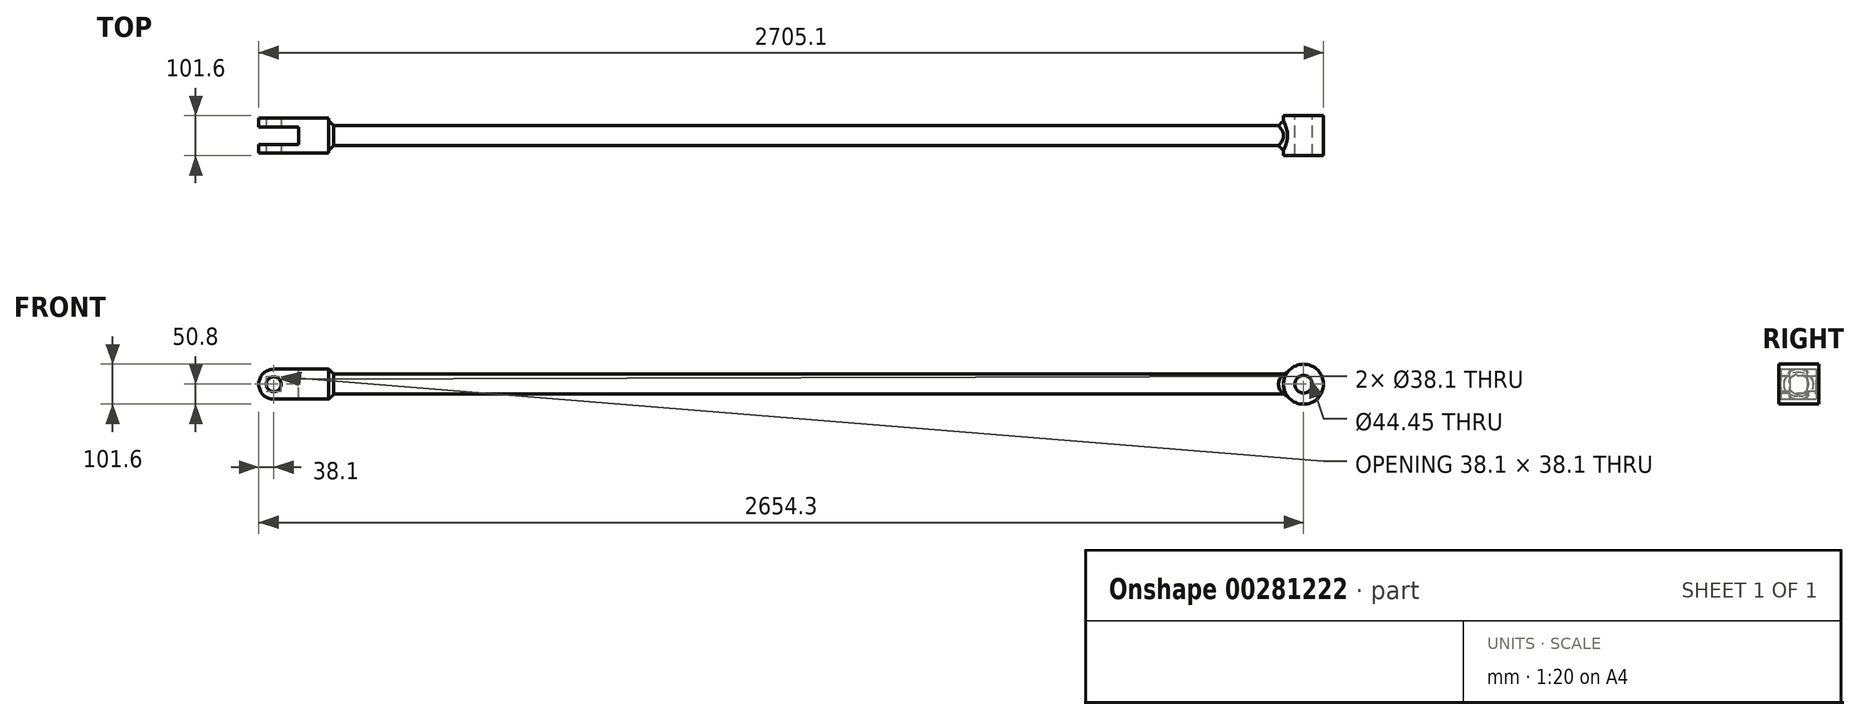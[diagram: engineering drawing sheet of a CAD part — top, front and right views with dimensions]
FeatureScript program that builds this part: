
annotation { "Feature Type Name" : "Feature", "Feature Type Description" : "" }
export const myFeature = defineFeature(function(context is Context, id is Id, definition is map)
    precondition{}
    {
        {
            var Q0;
            Q0=qCreatedBy(makeId("Front.planeOp"),FACE);
            var sketch = newSketch(context, id + "F0", { "sketchPlane" : qUnion([Q0])});
            skCircle(sketch, "E0", {"center": v(0, 0) * mm, "radius": 22.23 * mm});
            skCircle(sketch, "E1", {"center": v(0, 0) * mm, "radius": 50.8 * mm});
            skSolve(sketch);
        }
        {
            var Q0;
            Q0 = qSketchRegion(id + "F0", true);
            extrude(context, id + "F1", {"entities" : qUnion([Q0]), "endBound" : BoundingType.SYMMETRIC, "depth" : 101.6 * mm});
        }
        {
            var Q0;
            Q0=qCreatedBy(makeId("Right.planeOp"),FACE);
            var sketch = newSketch(context, id + "F2", { "sketchPlane" : qUnion([Q0])});
            skCircle(sketch, "E2", {"center": v(0, 0) * mm, "radius": 25.4 * mm});
            skSolve(sketch);
        }
        {
            var Q0;
            Q0 = qSketchRegion(id + "F2", true);
            extrude(context, id + "F3", {"entities" : qUnion([Q0]), "operationType" : NewBodyOperationType.ADD, "oppositeDirection" : true, "depth" : 2616.2 * mm});
        }
        {
            var Q0;
            Q0=qCreatedBy(makeId("Front.planeOp"),FACE);
            var sketch = newSketch(context, id + "F4", { "sketchPlane" : qUnion([Q0])});
            skLineSegment(sketch, "E3.0", {"start": v(-2616.2, 38.1) * mm, "end": v(-2616.2, -38.1) * mm, "construction": true});
            skCircle(sketch, "E4", {"center": v(-2616.2, 0) * mm, "radius": 38.1 * mm});
            skPoint(sketch, "E5.orphan", {"position": v(-2616.2, 25.4) * mm});
            skPoint(sketch, "E6.orphan", {"position": v(-2616.2, -25.4) * mm});
            skLineSegment(sketch, "E7.bottom", {"start": v(-2616.2, 38.1) * mm, "end": v(-2476.5, 38.1) * mm});
            skLineSegment(sketch, "E7.top", {"start": v(-2616.2, -38.1) * mm, "end": v(-2476.5, -38.1) * mm});
            skLineSegment(sketch, "E7.left", {"start": v(-2616.2, 38.1) * mm, "end": v(-2616.2, -38.1) * mm});
            skLineSegment(sketch, "E7.right", {"start": v(-2476.5, 38.1) * mm, "end": v(-2476.5, -38.1) * mm});
            skSolve(sketch);
        }
        {
            var Q0;
            Q0 = qSketchRegion(id + "F4", true);
            extrude(context, id + "F5", {"entities" : qUnion([Q0]), "operationType" : NewBodyOperationType.ADD, "endBound" : BoundingType.SYMMETRIC, "depth" : 88.9 * mm});
        }
        {
            var Q0;
            Q0=makeQuery(id+"F5.opExtrude","CAP_FACE",FACE,{"disambiguationData":[OSD([sQuery(id+"F4.wireOp",EDGE,"E4"),sQuery(id+"F4.wireOp",EDGE,"E7.bottom"),sQuery(id+"F4.wireOp",EDGE,"E7.top"),sQuery(id+"F4.wireOp",EDGE,"E7.right")])],"isStart":false});
            var sketch = newSketch(context, id + "F6", { "sketchPlane" : qUnion([Q0])});
            skArc(sketch, "E8.0.0", {"start": v(-2616.2, 38.1) * mm, "mid": v(-2654.3, 0) * mm, "end": v(-2616.2, -38.1) * mm, "construction": true});
            skLineSegment(sketch, "E8.0.1", {"start": v(-2616.2, -38.1) * mm, "end": v(-2476.5, -38.1) * mm, "construction": true});
            skLineSegment(sketch, "E8.0.2", {"start": v(-2476.5, -38.1) * mm, "end": v(-2476.5, 38.1) * mm, "construction": true});
            skLineSegment(sketch, "E8.0.3", {"start": v(-2476.5, 38.1) * mm, "end": v(-2616.2, 38.1) * mm, "construction": true});
            skCircle(sketch, "E9", {"center": v(-2616.2, 0) * mm, "radius": 19.05 * mm});
            skSolve(sketch);
        }
        {
            var Q0;
            Q0 = qSketchRegion(id + "F6", true);
            extrude(context, id + "F7", {"entities" : qUnion([Q0]), "operationType" : NewBodyOperationType.REMOVE, "endBound" : BoundingType.THROUGH_ALL, "oppositeDirection" : true, "depth" : 25.4 * mm});
        }
        {
            var Q0;
            Q0=makeQuery(id+"F5.opExtrude","SWEPT_FACE",FACE,{"disambiguationData":[OSD([sQuery(id+"F4.wireOp",EDGE,"E7.bottom")])]});
            var sketch = newSketch(context, id + "F8", { "sketchPlane" : qUnion([Q0])});
            skLineSegment(sketch, "E10", {"start": v(-2635.25, -44.45) * mm, "end": v(-2635.25, 44.45) * mm, "construction": true});
            skLineSegment(sketch, "E11", {"start": v(-2597.15, 44.45) * mm, "end": v(-2597.15, -44.45) * mm, "construction": true});
            skLineSegment(sketch, "E12", {"start": v(-2635.25, 0) * mm, "end": v(-2597.15, 0) * mm, "construction": true});
            skLineSegment(sketch, "E13", {"start": v(-2616.2, 0) * mm, "end": v(-2616.2, 76.94) * mm, "construction": true});
            skLineSegment(sketch, "E14.0", {"start": v(-2552.7, 0) * mm, "end": v(-2552.7, 76.94) * mm, "construction": true});
            skLineSegment(sketch, "E15.0", {"start": v(-2635.25, -22.35) * mm, "end": v(-2552.7, -22.35) * mm, "construction": true});
            skLineSegment(sketch, "E16.bottom", {"start": v(-2552.7, -22.35) * mm, "end": v(-2705.1, -22.35) * mm});
            skLineSegment(sketch, "E16.top", {"start": v(-2552.7, 22.1) * mm, "end": v(-2705.1, 22.1) * mm});
            skLineSegment(sketch, "E16.left", {"start": v(-2552.7, -22.35) * mm, "end": v(-2552.7, 22.1) * mm});
            skLineSegment(sketch, "E16.right", {"start": v(-2705.1, -22.35) * mm, "end": v(-2705.1, 22.1) * mm});
            skSolve(sketch);
        }
        {
            var Q0;
            Q0 = qSketchRegion(id + "F8", true);
            extrude(context, id + "F9", {"entities" : qUnion([Q0]), "operationType" : NewBodyOperationType.REMOVE, "endBound" : BoundingType.THROUGH_ALL, "oppositeDirection" : true, "depth" : 25.4 * mm});
        }
        {
            var Q0;
            Q0=makeQuery(id+"F1.opExtrude","CAP_FACE",FACE,{"disambiguationData":[OSD([sQuery(id+"F0.wireOp",EDGE,"E0"),sQuery(id+"F0.wireOp",EDGE,"E1")])],"isStart":false});
            var sketch = newSketch(context, id + "F10", { "sketchPlane" : qUnion([Q0])});
            skCircle(sketch, "E17.0", {"center": v(0, 0) * mm, "radius": 22.23 * mm});
            skSolve(sketch);
        }
        {
            var Q0;
            Q0 = qSketchRegion(id + "F10", true);
            extrude(context, id + "F11", {"entities" : qUnion([Q0]), "operationType" : NewBodyOperationType.REMOVE, "endBound" : BoundingType.THROUGH_ALL, "oppositeDirection" : true, "depth" : 25.4 * mm});
        }
        {
            var Q0;
            Q0=makeQuery(id+"F3.boolean.opBoolean","INTERSECT",EDGE,{"derivedFrom":[makeQuery(id+"F1.opExtrude","SWEPT_FACE",FACE,{"disambiguationData":[OSD([sQuery(id+"F0.wireOp",EDGE,"E1")])]}),makeQuery(id+"F3.opExtrude","SWEPT_FACE",FACE,{"disambiguationData":[OSD([sQuery(id+"F2.wireOp",EDGE,"E2")])]})]});
            chamfer(context, id + "F12", {"entities" : qUnion([Q0]), "width" : 12.7 * mm, "tangentPropagation" : true});
        }
        {
            var Q0;
            {var subQ0=sQuery(id+"F2.wireOp",EDGE,"E2");Q0=makeQuery(id+"F5.boolean.opBoolean","INTERSECT",EDGE,{"derivedFrom":[makeQuery(id+"F3.boolean.opBoolean","SPLIT",FACE,{"disambiguationData":[TD([makeQuery(id+"F1.opExtrude","SWEPT_FACE",FACE,{"disambiguationData":[OSD([sQuery(id+"F0.wireOp",EDGE,"E1")])]}),makeQuery(id+"F3.opExtrude","CAP_FACE",FACE,{"disambiguationData":[OSD([subQ0])],"isStart":false})])],"derivedFrom":makeQuery(id+"F3.opExtrude","SWEPT_FACE",FACE,{"disambiguationData":[OSD([subQ0])]})}),makeQuery(id+"F5.opExtrude","SWEPT_FACE",FACE,{"disambiguationData":[OSD([sQuery(id+"F4.wireOp",EDGE,"E7.right")])]})]});}
            chamfer(context, id + "F13", {"entities" : qUnion([Q0]), "width" : 12.7 * mm, "tangentPropagation" : true});
        }
    });
